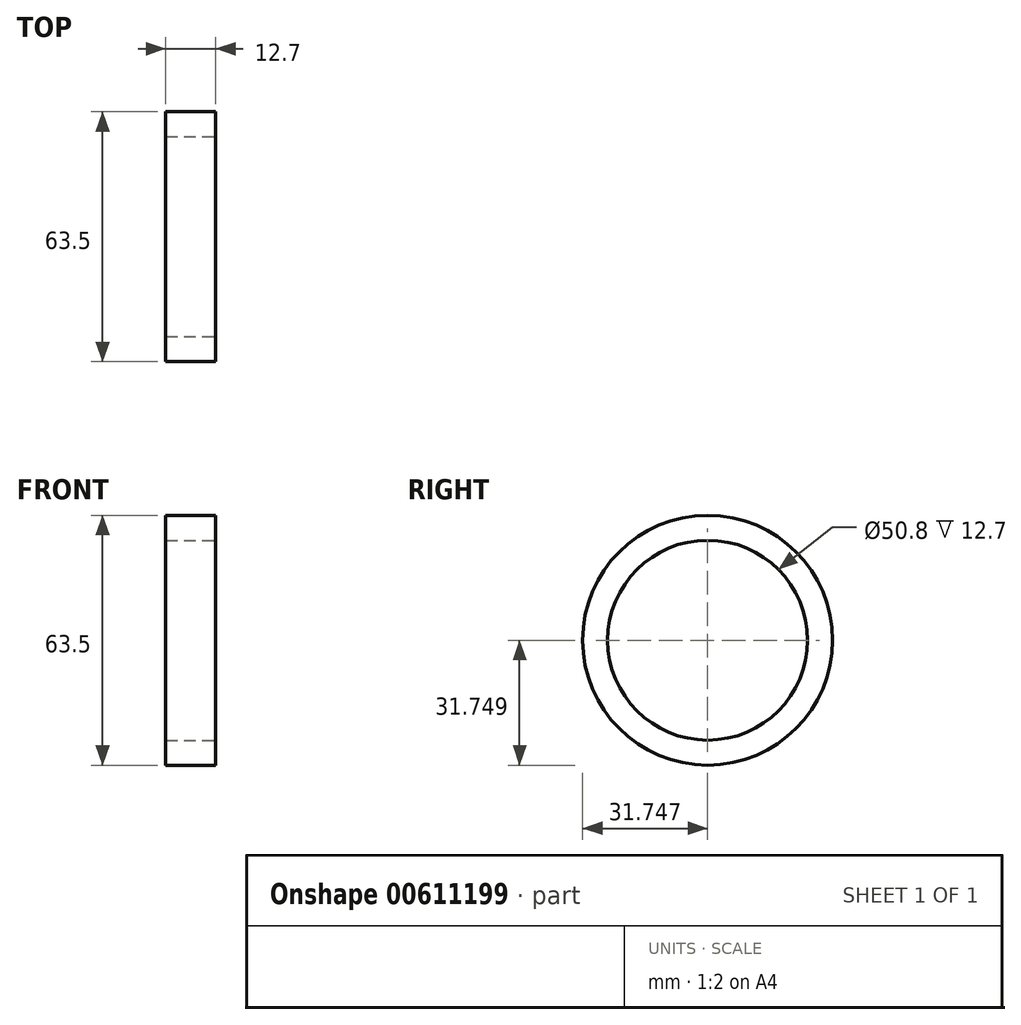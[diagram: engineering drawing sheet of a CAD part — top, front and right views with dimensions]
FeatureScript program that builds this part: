
annotation { "Feature Type Name" : "Feature", "Feature Type Description" : "" }
export const myFeature = defineFeature(function(context is Context, id is Id, definition is map)
    precondition{}
    {
        {
            var Q0;
            Q0=qCreatedBy(makeId("Right.planeOp"),FACE);
            var sketch = newSketch(context, id + "F0", { "sketchPlane" : qUnion([Q0])});
            skCircle(sketch, "E0", {"center": v(-2.3, 0.77) * mm, "radius": 31.75 * mm});
            skSolve(sketch);
        }
        {
            var Q0;
            Q0 = qSketchRegion(id + "F0", true);
            extrude(context, id + "F1", {"entities" : qUnion([Q0]), "depth" : 12.7 * mm, "offsetDistance" : 25.4 * mm});
        }
        {
            var Q0;
            Q0=makeQuery(id+"F1.opExtrude","CAP_FACE",FACE,{"disambiguationData":[OSD([sQuery(id+"F0.wireOp",EDGE,"E0")])],"isStart":false});
            var sketch = newSketch(context, id + "F2", { "sketchPlane" : qUnion([Q0])});
            skCircle(sketch, "E1", {"center": v(-2.3, 0.77) * mm, "radius": 25.4 * mm});
            skSolve(sketch);
        }
        {
            var Q0;
            Q0=sQuery(id+"F2.wireOp",VERTEX,"E1.center");
            var Q1;
            Q1=makeQuery(id+"F1.opExtrude","SWEPT_BODY",BODY,{"disambiguationData":[OSD([sQuery(id+"F0.wireOp",EDGE,"E0")])]});
            hole(context, id + "F3", {"style" : HoleStyle.SIMPLE, "endStyle" : HoleEndStyle.THROUGH, "holeDiameter" : 50.8 * mm, "majorDiameter" : 6.35 * mm, "isTappedThrough" : true, "tappedDepth" : 12.7 * mm, "tapClearance" : 3, "locations" : qUnion([Q0]), "scope" : qUnion([Q1])});
        }
    });
